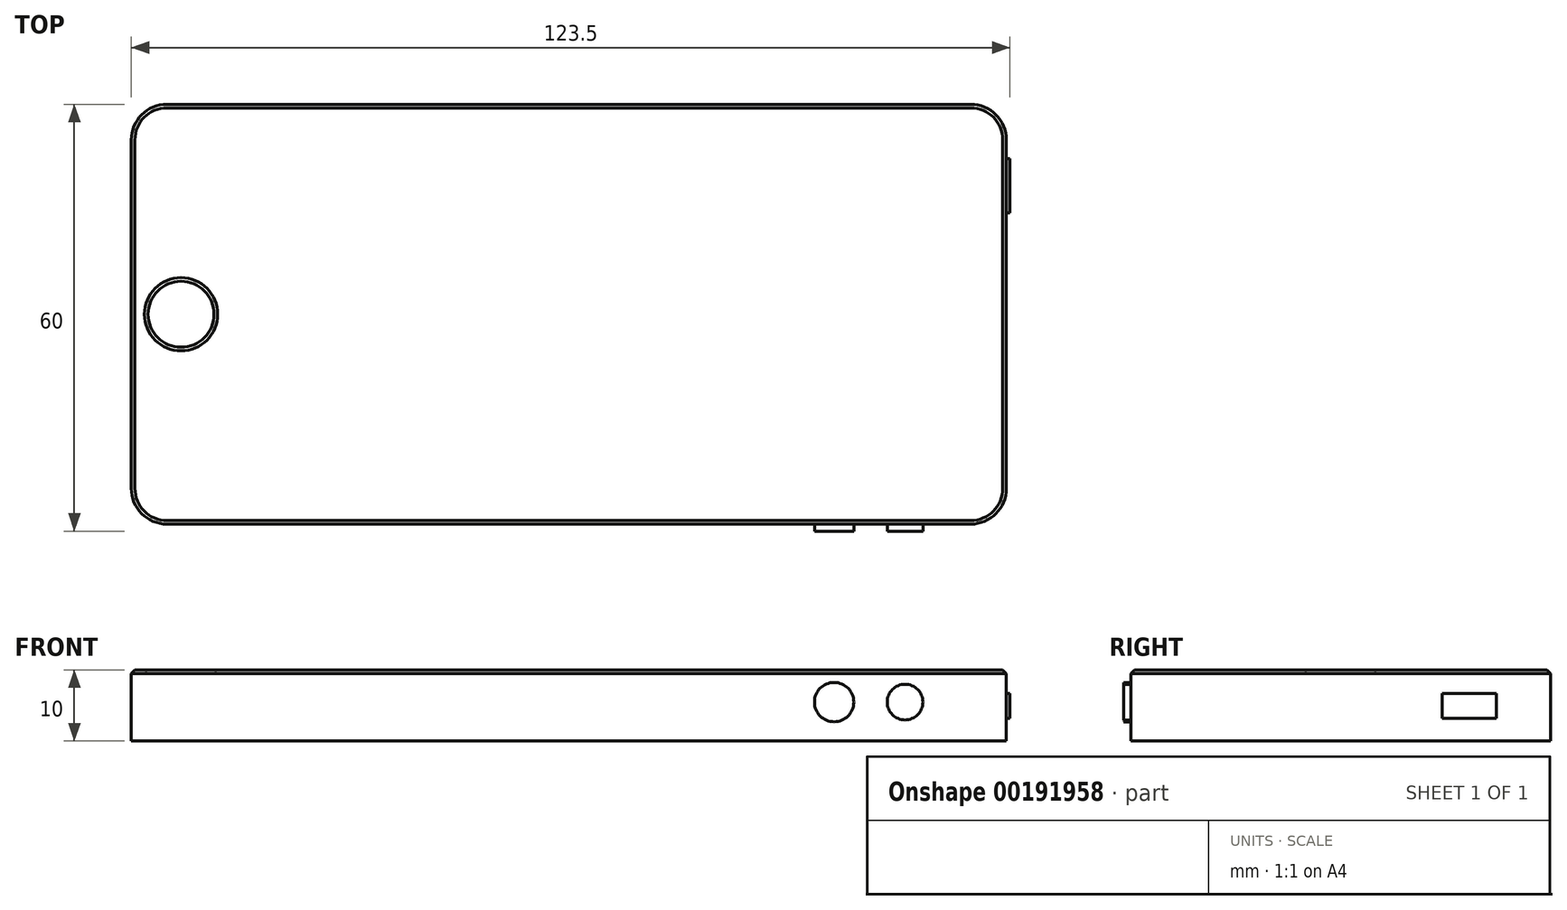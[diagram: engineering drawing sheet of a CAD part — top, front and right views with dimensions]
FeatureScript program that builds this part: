
annotation { "Feature Type Name" : "Feature", "Feature Type Description" : "" }
export const myFeature = defineFeature(function(context is Context, id is Id, definition is map)
    precondition{}
    {
        {
            var Q0;
            Q0=qCreatedBy(makeId("Top.planeOp"),FACE);
            var sketch = newSketch(context, id + "F0", { "sketchPlane" : qUnion([Q0])});
            skLineSegment(sketch, "E0.bottom", {"start": v(-61.5, 29.5) * mm, "end": v(61.5, 29.5) * mm});
            skLineSegment(sketch, "E0.top", {"start": v(-61.5, -29.5) * mm, "end": v(61.5, -29.5) * mm});
            skLineSegment(sketch, "E0.left", {"start": v(-61.5, 29.5) * mm, "end": v(-61.5, -29.5) * mm});
            skLineSegment(sketch, "E0.right", {"start": v(61.5, 29.5) * mm, "end": v(61.5, -29.5) * mm});
            skPoint(sketch, "E0.middle", {"position": v(0, 0) * mm});
            skSolve(sketch);
        }
        {
            var Q0;
            Q0=makeQuery(id+"F0.imprint","IMPRINT",FACE,{"disambiguationData":[TD([[makeQuery(id+"F0.imprint","IMPRINT",EDGE,{"derivedFrom":sQuery(id+"F0.wireOp",EDGE,"E0.bottom")}),-1.0]])]});
            extrude(context, id + "F1", {"entities" : qUnion([Q0]), "depth" : 10 * mm});
        }
        {
            var Q0;
            Q0=makeQuery(id+"F1.opExtrude","SWEPT_EDGE",EDGE,{"disambiguationData":[OSD([sQuery(id+"F0.wireOp",EDGE,"E0.bottom"),sQuery(id+"F0.wireOp",EDGE,"E0.left")])]});
            var Q1;
            Q1=makeQuery(id+"F1.opExtrude","SWEPT_EDGE",EDGE,{"disambiguationData":[OSD([sQuery(id+"F0.wireOp",EDGE,"E0.bottom"),sQuery(id+"F0.wireOp",EDGE,"E0.right")])]});
            fillet(context, id + "F2", {"entities" : qUnion([Q0, Q1]), "radius" : 5 * mm, "tangentPropagation" : true, "allowEdgeOverflow" : false});
        }
        {
            var Q0;
            Q0=makeQuery(id+"F1.opExtrude","SWEPT_EDGE",EDGE,{"disambiguationData":[OSD([sQuery(id+"F0.wireOp",EDGE,"E0.top"),sQuery(id+"F0.wireOp",EDGE,"E0.left")])]});
            var Q1;
            Q1=makeQuery(id+"F1.opExtrude","SWEPT_EDGE",EDGE,{"disambiguationData":[OSD([sQuery(id+"F0.wireOp",EDGE,"E0.top"),sQuery(id+"F0.wireOp",EDGE,"E0.right")])]});
            fillet(context, id + "F3", {"entities" : qUnion([Q0, Q1]), "radius" : 5 * mm, "tangentPropagation" : true, "allowEdgeOverflow" : false});
        }
        {
            var Q0;
            Q0=makeQuery(id+"F1.opExtrude","SWEPT_FACE",FACE,{"disambiguationData":[OSD([sQuery(id+"F0.wireOp",EDGE,"E0.top")])]});
            var sketch = newSketch(context, id + "F4", { "sketchPlane" : qUnion([Q0])});
            skCircle(sketch, "E1", {"center": v(47.26, 5.47) * mm, "radius": 2.5 * mm});
            skCircle(sketch, "E2", {"center": v(37.3, 5.47) * mm, "radius": 2.77 * mm});
            skSolve(sketch);
        }
        {
            var Q0;
            Q0=makeQuery(id+"F4.imprint","IMPRINT",FACE,{"disambiguationData":[TD([[makeQuery(id+"F4.imprint","IMPRINT",EDGE,{"derivedFrom":sQuery(id+"F4.wireOp",EDGE,"E2")}),1.0]])]});
            var Q1;
            Q1=makeQuery(id+"F4.imprint","IMPRINT",FACE,{"disambiguationData":[TD([[makeQuery(id+"F4.imprint","IMPRINT",EDGE,{"derivedFrom":sQuery(id+"F4.wireOp",EDGE,"E1")}),1.0]])]});
            extrude(context, id + "F5", {"entities" : qUnion([Q0, Q1]), "operationType" : NewBodyOperationType.ADD, "depth" : 1 * mm});
        }
        {
            var Q0;
            Q0=makeQuery(id+"F1.opExtrude","SWEPT_FACE",FACE,{"disambiguationData":[OSD([sQuery(id+"F0.wireOp",EDGE,"E0.right")])]});
            var sketch = newSketch(context, id + "F6", { "sketchPlane" : qUnion([Q0])});
            skLineSegment(sketch, "E3.bottom", {"start": v(21.9, 6.7) * mm, "end": v(14.27, 6.7) * mm});
            skLineSegment(sketch, "E3.top", {"start": v(21.9, 3.18) * mm, "end": v(14.27, 3.18) * mm});
            skLineSegment(sketch, "E3.left", {"start": v(21.9, 6.7) * mm, "end": v(21.9, 3.18) * mm});
            skLineSegment(sketch, "E3.right", {"start": v(14.27, 6.7) * mm, "end": v(14.27, 3.18) * mm});
            skPoint(sketch, "E3.middle", {"position": v(18.08, 4.94) * mm});
            skSolve(sketch);
        }
        {
            var Q0;
            Q0 = qSketchRegion(id + "F6", true);
            extrude(context, id + "F7", {"entities" : qUnion([Q0]), "operationType" : NewBodyOperationType.ADD, "depth" : .5 * mm});
        }
        {
            var Q0;
            Q0=makeQuery(id+"F1.opExtrude","CAP_FACE",FACE,{"disambiguationData":[OSD([sQuery(id+"F0.wireOp",EDGE,"E0.bottom"),sQuery(id+"F0.wireOp",EDGE,"E0.top"),sQuery(id+"F0.wireOp",EDGE,"E0.left"),sQuery(id+"F0.wireOp",EDGE,"E0.right")])],"isStart":false});
            var sketch = newSketch(context, id + "F8", { "sketchPlane" : qUnion([Q0])});
            skCircle(sketch, "E4", {"center": v(-54.51, 0) * mm, "radius": 4.64 * mm});
            skSolve(sketch);
        }
        {
            var Q0;
            Q0 = qSketchRegion(id + "F8", true);
            extrude(context, id + "F9", {"entities" : qUnion([Q0]), "operationType" : NewBodyOperationType.REMOVE, "oppositeDirection" : true, "depth" : .5 * mm});
        }
        {
            var Q0;
            Q0=makeQuery(id+"F1.opExtrude","CAP_FACE",FACE,{"disambiguationData":[OSD([sQuery(id+"F0.wireOp",EDGE,"E0.bottom"),sQuery(id+"F0.wireOp",EDGE,"E0.top"),sQuery(id+"F0.wireOp",EDGE,"E0.left"),sQuery(id+"F0.wireOp",EDGE,"E0.right")])],"isStart":false});
            chamfer(context, id + "F10", {"entities" : qUnion([Q0]), "width" : .5 * mm, "tangentPropagation" : true});
        }
    });
